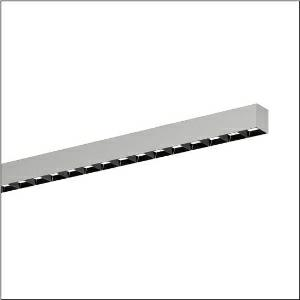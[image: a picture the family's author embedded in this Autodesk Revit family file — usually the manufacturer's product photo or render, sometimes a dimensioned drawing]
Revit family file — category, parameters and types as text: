
# Revit family: silica_r__21_51mx24tctas_d744
name_source: partatom
category: Lighting Fixtures
units: mm (PartAtom-declared; Revit-internal decimal feet)

## family parameters
Cut with Voids When Loaded = No
Host = Face
Light Source = No
Part Type = Normal
Room Calculation Point = No
Round Connector Dimension = Use Diameter
Shared = No

## types (1)
- --- (1 x LED, 8200 lm, 81.1 W, 6500K)
    Apparent Load = 81 VA
    CIE Flux Codes = 74 94 99 100 100
    Color Rendering = 80
    Color Temperature = 6500K
    Default Elevation = 1800 mm
    Description = Silica® 21, office luminaire, primary light control with darklight reflector, of PMMA, black, light emission: direct distribution, primary light characteristic: asymmetric, installation type: surface-mounted, LED, rated luminous flux: 8.200lm, luminous efficacy: 96lm/W, light colour: 8tw, colour temperature: 2700..6500K, control gear: DALI DT8, with terminal, 3+2-pole, max. 2.5mm², mains connection: 220..240V, AC, 50/60Hz, rated input power: 85.2W, luminaire housing, of aluminium, metallic grey (RAL 9006), length: 3.004mm, width: 53mm, height: 53mm, protection rating (complete): IP20, insulation class (complete): insulation class I (protective earthing), certification: CE, permissible operating ambient temperature: 0..+35°C, standard: EN 50419, packaging unit: 1 piece
    Height = 53 mm
    Lamp = 1 x LED
    Lamp Light Flux = 8200 lm
    Lamp Power = 81.1 W
    Lamp count = 1
    Length = 3004 mm
    Luminous efficacy = 101 lm/W
    Manufacturer = Siteco
    ModVariant = No
    Model = 51MX24TCTAS
    Mounting Place = Ceiling
    Mounting Type = Surface mounted
    Number of Poles = 1
    OnlyDefault = Yes
    Power Factor = 1
    Product Name = Silica® 21
    Product group = office luminaire | ceiling mounted
    ProductGroupID = 303
    Protection Class = Protection class I
    Protection Degree = IP 20
    RLX_Detail_Level = 1
    RLX_Emergency_Light_Flux = 0 lm
    RLX_Emergency_Type = 0
    RLX_Emergency_Type_DB = No
    RlxData = <blob elided: 60285 chars, md5=b5280140>
    Socket = socket
    Standby Power = 0 W
    System Light Flux = 8200 lm
    System Power = 81 W
    Type Comments = individual setting
    Type Image = l_1335929.jpg
    URL = http://relux.com
    VarID = @adj_161447
    Voltage = 0 V
    Weight = 0.00 kg
    Width = 53 mm

## geometry (parser evidence)
native form markers: Blend x4, Sweep x11
no freeform markers — native parametric forms only
